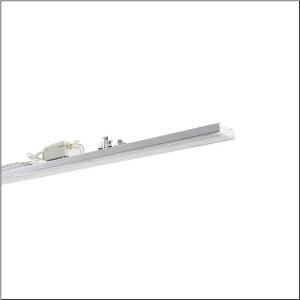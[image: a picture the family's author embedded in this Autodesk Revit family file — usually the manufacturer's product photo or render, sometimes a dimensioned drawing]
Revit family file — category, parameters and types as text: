
# Revit family: licross_r__21_recessed_mo_52tl18de445g_1bd1
name_source: partatom
category: Lighting Fixtures
units: mm (PartAtom-declared; Revit-internal decimal feet)

## family parameters
Cut with Voids When Loaded = No
Host = Face
Light Source = No
Part Type = Normal
Room Calculation Point = No
Round Connector Dimension = Use Diameter
Shared = No

## types (1)
- --- (1 x LED, 4990 lm, 29.9 W, 4000K)
    Apparent Load = 30 VA
    CIE Flux Codes = 79 95 99 100 100
    Color Rendering = 80
    Color Temperature = 4000K
    Default Elevation = 1800 mm
    Description = Licross® 21 Recessed MO, luminaire insert, of sheet steel, galvanised, coil coated, white, length: 750mm, width: 66mm, height: 67mm, LED rated luminous flux: 4.990lm, light colour: 840, control gear: DALI 2, with plug, 5-pole, with phase selection, mains connection: 220..240V, AC, 50/60Hz, rated input power: 30W, halogen-free wiring, primary light control with lens, of plastic, primary optical cover: cover, of PMMA, light emission: direct distribution, primary light characteristic: symmetric, protection rating (complete): IP40, insulation class (complete): insulation class I (protective earthing), certification: CE, ENEC, VDE, UKCA, protection symbol: D if used in an environment without relevant dust loads with corresponding accessories, impact resistance: IK06, permissible ambient temperature for indoor applications: -25..+35°C, corresponds to IFS (International Featured Standards) requirements for safety and quality in the food industry, reducing of maximum allowable ambient temperature of 5°C with ceiling mounting, LABS conformity tested according to VDMA 24364:2018-05, packaging unit: 1 piece
    Height = 58 mm
    Lamp = 1 x LED
    Lamp Light Flux = 4990 lm
    Lamp Power = 29.9 W
    Lamp count = 1
    Length = 750 mm
    Luminous efficacy = 167 lm/W
    Manufacturer = Siteco
    ModVariant = No
    Model = 52TL18DE445G
    Mounting Place = Ceiling
    Mounting Type = Pendant
    Number of Poles = 1
    OnlyDefault = Yes
    Power Factor = 1
    Product Name = Licross® 21 Recessed MO
    Product group = luminaire insert
    ProductGroupID = 901
    Protection Class = Protection class I
    Protection Degree = IP 40
    RLX_Detail_Level = 1
    RLX_Emergency_Light_Flux = 0 lm
    RLX_Emergency_Type = 0
    RLX_Emergency_Type_DB = No
    RlxData = <blob elided: 28913 chars, md5=a5b58f0e>
    Socket = socket
    Standby Power = 0 W
    System Light Flux = 4990 lm
    System Power = 30 W
    Type Comments = factory setting: luminous flux: 100 % | dim-lin: 254 | 390 mA
    Type Image = l_1296930.jpg
    URL = http://relux.com
    VarID = @adj_057627
    Voltage = 0 V
    Weight = 0.00 kg
    Width = 66 mm

## geometry (parser evidence)
native form markers: Blend x4, Sweep x10
no freeform markers — native parametric forms only
